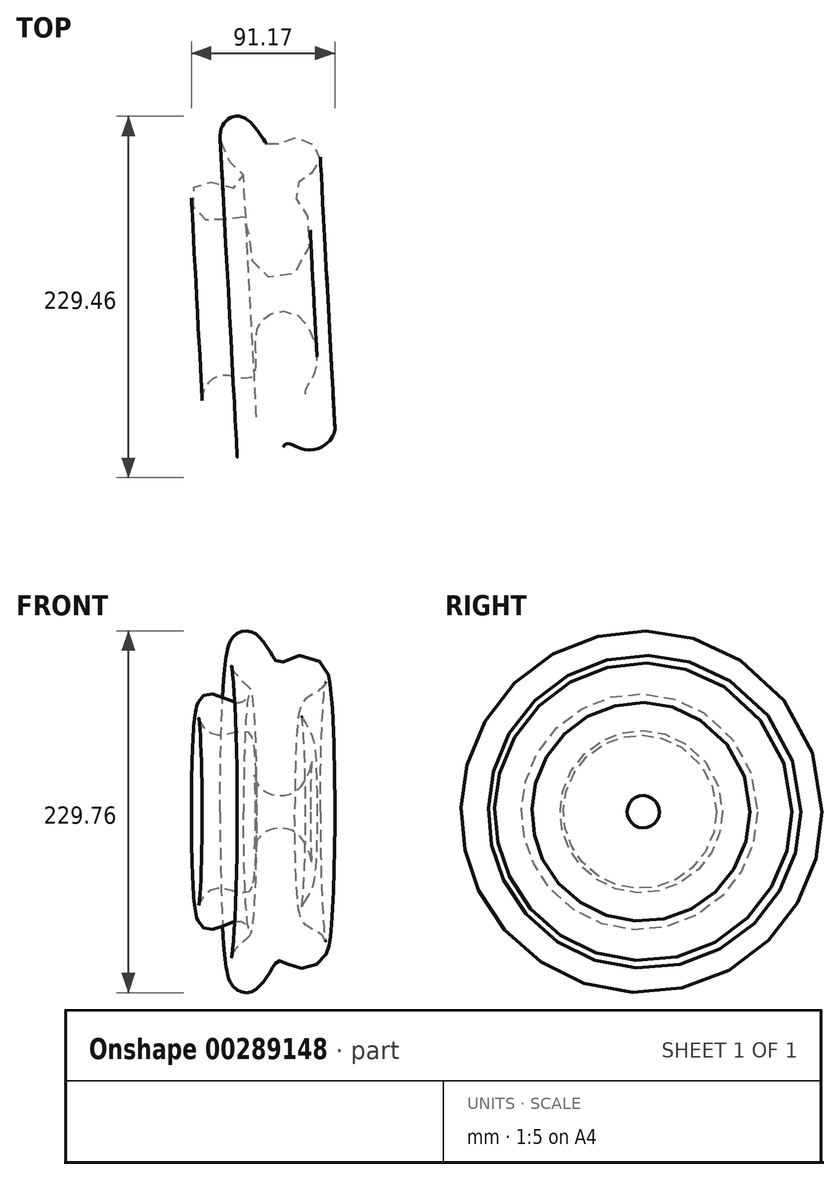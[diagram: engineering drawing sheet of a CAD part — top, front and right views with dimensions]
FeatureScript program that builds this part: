
annotation { "Feature Type Name" : "Feature", "Feature Type Description" : "" }
export const myFeature = defineFeature(function(context is Context, id is Id, definition is map)
    precondition{}
    {
        {
            var Q0;
            Q0=qCreatedBy(makeId("Top.planeOp"),FACE);
            var sketch = newSketch(context, id + "F0", { "sketchPlane" : qUnion([Q0])});
            skFitSpline(sketch, "E0", {"points": [v(0, 30.8) * mm, v(3.95, 29.18) * mm, v(15.62, 34.4) * mm, v(29.45, 30.44) * mm, v(34.12, 21.46) * mm, v(29.45, 12.84) * mm, v(21.37, 7.45) * mm, v(18.14, -2.6) * mm, v(26.58, -17.33) * mm, v(17.96, -51.63) * mm, v(-4.49, -50.91) * mm, v(-10.6, -30.62) * mm, v(-14.9, -15.53) * mm, v(-30.7, -18.59) * mm, v(-42.02, -15.35) * mm, v(-47.77, -2.42) * mm, v(-40.23, 7.1) * mm, v(-21.01, 2.6) * mm, v(-14.73, 10.87) * mm, v(-24.96, 20.74) * mm, v(-27.66, 42.83) * mm, v(-14.19, 47.14) * mm, v(0, 30.8) * mm]});
            skLineSegment(sketch, "E1", {"start": v(14.94, 69.55) * mm, "end": v(-24.58, 69.55) * mm});
            skLineSegment(sketch, "E2", {"start": v(-19.4, -66.9) * mm, "end": v(25.14, -64.5) * mm});
            skSolve(sketch);
        }
        {
            var Q0;
            Q0=makeQuery(id+"F0.imprint","IMPRINT",FACE,{"disambiguationData":[TD([[makeQuery(id+"F0.imprint","IMPRINT",EDGE,{"derivedFrom":sQuery(id+"F0.wireOp",EDGE,"E0")}),-1.0]])]});
            var Q1;
            Q1=sQuery(id+"F0.wireOp",EDGE,"E2");
            revolve(context, id + "F1", {"entities" : qUnion([Q0]), "axis" : qUnion([Q1]), "revolveType" : RevolveType.FULL});
        }
    });
